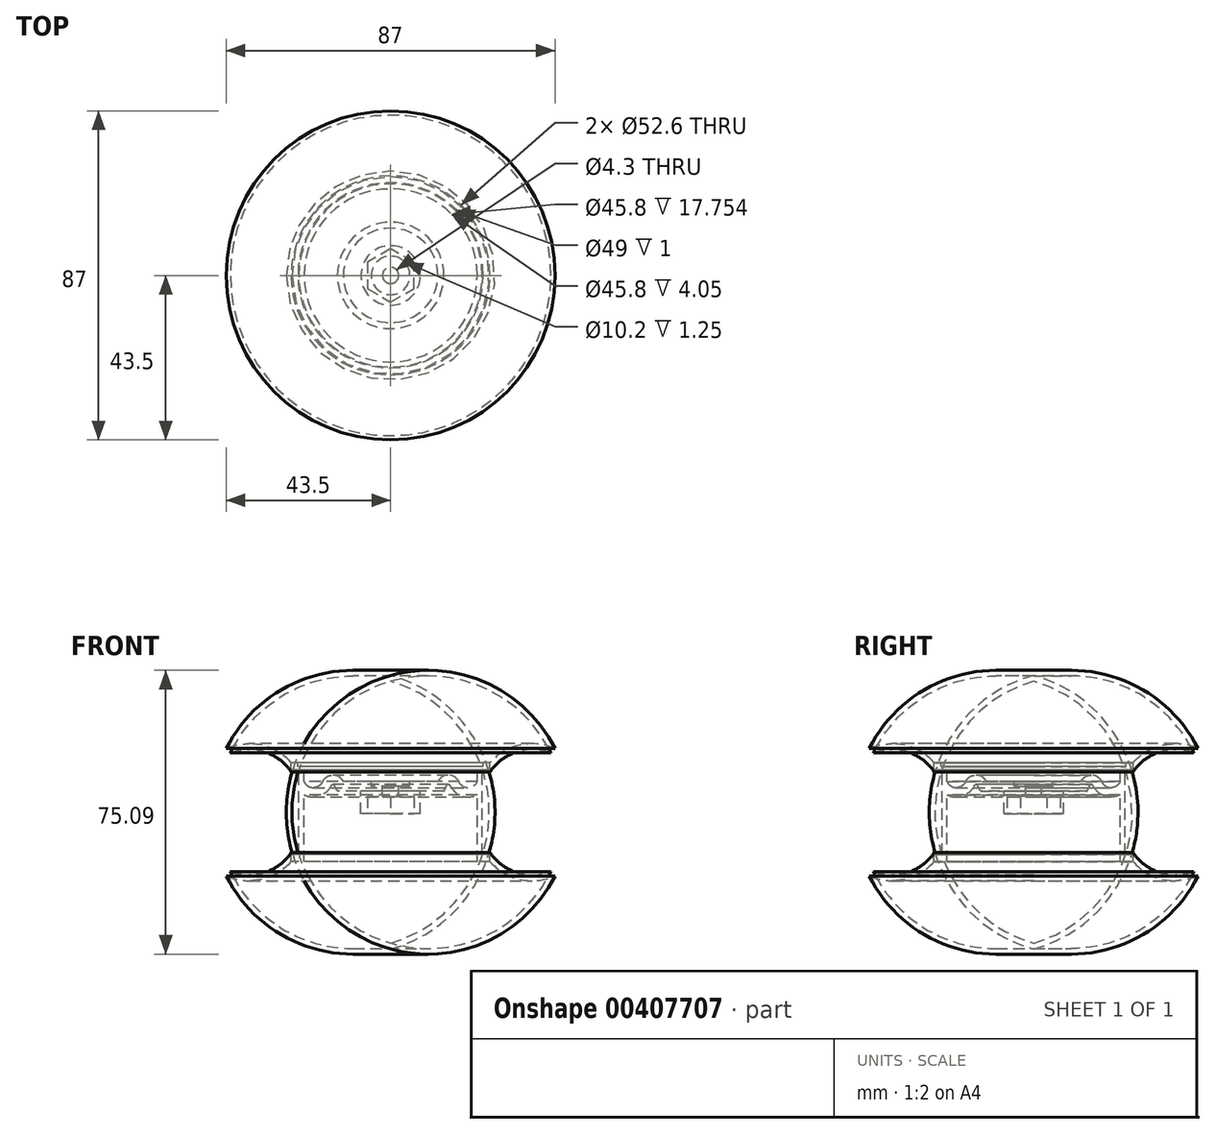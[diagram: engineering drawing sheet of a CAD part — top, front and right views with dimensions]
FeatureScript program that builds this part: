
annotation { "Feature Type Name" : "Feature", "Feature Type Description" : "" }
export const myFeature = defineFeature(function(context is Context, id is Id, definition is map)
    precondition{}
    {
        {
            var Q0;
            Q0=qCreatedBy(makeId("Front.planeOp"),FACE);
            var sketch = newSketch(context, id + "F0", { "sketchPlane" : qUnion([Q0])});
            skLineSegment(sketch, "E0", {"start": v(26.3, 0) * mm, "end": v(24.5, 0) * mm});
            skLineSegment(sketch, "E1", {"start": v(24.5, 0) * mm, "end": v(24.5, -1) * mm});
            skLineSegment(sketch, "E2", {"start": v(24.5, -1) * mm, "end": v(22.9, -1) * mm});
            skLineSegment(sketch, "E3", {"start": v(22.9, -1) * mm, "end": v(22.9, -26.25) * mm});
            skLineSegment(sketch, "E4", {"start": v(22.9, -26.25) * mm, "end": v(26.3, -26.25) * mm});
            skLineSegment(sketch, "E5", {"start": v(26.3, -26.25) * mm, "end": v(26.3, -24.35) * mm});
            skLineSegment(sketch, "E6", {"start": v(26.3, -24.35) * mm, "end": v(24.25, -24.35) * mm});
            skLineSegment(sketch, "E7", {"start": v(24.25, -24.35) * mm, "end": v(24.25, -1.9) * mm});
            skLineSegment(sketch, "E8", {"start": v(24.25, -1.9) * mm, "end": v(26.3, -1.9) * mm});
            skLineSegment(sketch, "E9", {"start": v(26.3, -1.9) * mm, "end": v(26.3, 0) * mm});
            skLineSegment(sketch, "E10", {"start": v(0, 0) * mm, "end": v(0, -26.25) * mm});
            skSolve(sketch);
        }
        {
            var Q0;
            Q0=qCreatedBy(makeId("Front.planeOp"),FACE);
            var sketch = newSketch(context, id + "F1", { "sketchPlane" : qUnion([Q0])});
            skLineSegment(sketch, "E11", {"start": v(2.15, -13.55) * mm, "end": v(2.15, -6.3) * mm});
            skLineSegment(sketch, "E12", {"start": v(2.15, -6.3) * mm, "end": v(5.1, -6.3) * mm});
            skLineSegment(sketch, "E13", {"start": v(5.1, -6.3) * mm, "end": v(5.1, -5.05) * mm});
            skLineSegment(sketch, "E14", {"start": v(5.1, -5.05) * mm, "end": v(12.5, -5.05) * mm});
            skLineSegment(sketch, "E15", {"start": v(2.15, -13.55) * mm, "end": v(7.88, -13.55) * mm});
            skLineSegment(sketch, "E16", {"start": v(7.88, -13.55) * mm, "end": v(7.88, -7.55) * mm});
            skLineSegment(sketch, "E17", {"start": v(7.88, -7.55) * mm, "end": v(14.1, -7.55) * mm});
            skArc(sketch, "E18", {"start": v(18, -5.05) * mm, "mid": v(15.25, -3.3) * mm, "end": v(12.5, -5.05) * mm});
            skArc(sketch, "E19", {"start": v(18, -5.05) * mm, "mid": v(20.45, -6.6) * mm, "end": v(22.9, -5.05) * mm});
            skArc(sketch, "E20.0", {"start": v(15.74, -6.1) * mm, "mid": v(15.25, -5.8) * mm, "end": v(14.76, -6.1) * mm});
            skArc(sketch, "E20.1", {"start": v(15.74, -6.1) * mm, "mid": v(18.8, -8.84) * mm, "end": v(22.9, -8.5) * mm});
            skLineSegment(sketch, "E21", {"start": v(14.76, -6.1) * mm, "end": v(14.1, -7.55) * mm});
            skLineSegment(sketch, "E22", {"start": v(14.76, -6.1) * mm, "end": v(12.5, -5.05) * mm, "construction": true});
            skLineSegment(sketch, "E23", {"start": v(22.9, -5.05) * mm, "end": v(22.9, -8.5) * mm});
            skSolve(sketch);
        }
        {
            var Q0;
            Q0=makeQuery(id+"F0.imprint","IMPRINT",FACE,{"disambiguationData":[TD([[makeQuery(id+"F0.imprint","IMPRINT",EDGE,{"derivedFrom":sQuery(id+"F0.wireOp",EDGE,"E0")}),1.0]])]});
            var Q1;
            Q1=sQuery(id+"F0.wireOp",EDGE,"E10");
            revolve(context, id + "F2", {"entities" : qUnion([Q0]), "axis" : qUnion([Q1]), "revolveType" : RevolveType.FULL});
        }
        {
            var Q0;
            Q0 = qSketchRegion(id + "F1", true);
            var Q1;
            Q1=sQuery(id+"F0.wireOp",EDGE,"E10");
            revolve(context, id + "F3", {"operationType" : NewBodyOperationType.ADD, "entities" : qUnion([Q0]), "axis" : qUnion([Q1]), "revolveType" : RevolveType.FULL});
        }
        {
            var Q0;
            Q0=makeQuery(id+"F3.opRevolve","SWEPT_FACE",FACE,{"disambiguationData":[OSD([sQuery(id+"F1.wireOp",EDGE,"E15")])]});
            var sketch = newSketch(context, id + "F4", { "sketchPlane" : qUnion([Q0])});
            skCircle(sketch, "E24.cCircle", {"center": v(0, 0) * mm, "radius": 6.13 * mm, "construction": true});
            skLineSegment(sketch, "E24.0", {"start": v(0, 7.07) * mm, "end": v(6.13, 3.54) * mm});
            skLineSegment(sketch, "E24.1", {"start": v(6.12, 3.54) * mm, "end": v(6.12, -3.54) * mm});
            skLineSegment(sketch, "E24.2", {"start": v(6.12, -3.54) * mm, "end": v(0, -7.07) * mm});
            skLineSegment(sketch, "E24.3", {"start": v(0, -7.07) * mm, "end": v(-6.13, -3.54) * mm});
            skLineSegment(sketch, "E24.4", {"start": v(-6.13, -3.54) * mm, "end": v(-6.13, 3.54) * mm});
            skLineSegment(sketch, "E24.5", {"start": v(-6.12, 3.54) * mm, "end": v(0, 7.07) * mm});
            skPoint(sketch, "E24.0.midPoint", {"position": v(3.06, 5.3) * mm});
            skSolve(sketch);
        }
        {
            var Q0;
            Q0 = qSketchRegion(id + "F4", true);
            extrude(context, id + "F5", {"entities" : qUnion([Q0]), "operationType" : NewBodyOperationType.REMOVE, "oppositeDirection" : true, "depth" : 4.6 * mm});
        }
        {
            var Q0;
            Q0=qCreatedBy(makeId("Front.planeOp"),FACE);
            var sketch = newSketch(context, id + "F6", { "sketchPlane" : qUnion([Q0])});
            skArc(sketch, "E25", {"start": v(-26.3, 0) * mm, "mid": v(-34.3, 4.66) * mm, "end": v(-43.5, 3.74) * mm});
            skArc(sketch, "E26", {"start": v(-43.5, -29.99) * mm, "mid": v(-34.3, -30.9) * mm, "end": v(-26.3, -26.25) * mm});
            skLineSegment(sketch, "E27", {"start": v(24.5, 0) * mm, "end": v(26.3, 0) * mm});
            skLineSegment(sketch, "E28", {"start": v(-26.3, 0) * mm, "end": v(-24.5, 0) * mm, "construction": true});
            skLineSegment(sketch, "E29", {"start": v(-22.9, -26.25) * mm, "end": v(-26.3, -26.25) * mm, "construction": true});
            skLineSegment(sketch, "E30", {"start": v(26.3, -26.25) * mm, "end": v(22.9, -26.25) * mm});
            skArc(sketch, "E31", {"start": v(-43.5, 3.74) * mm, "mid": v(-47.5, -13.13) * mm, "end": v(-43.5, -29.99) * mm});
            skLineSegment(sketch, "E32", {"start": v(-43.5, -29.99) * mm, "end": v(-43.5, 3.74) * mm, "construction": true});
            skLineSegment(sketch, "E33", {"start": v(-37.48, -16.25) * mm, "end": v(-37.48, -10) * mm, "construction": true});
            skLineSegment(sketch, "E34", {"start": v(-26.3, 0) * mm, "end": v(-26.3, -26.25) * mm});
            skSolve(sketch);
        }
        {
            var Q0;
            Q0 = qSketchRegion(id + "F6", true);
            var Q1;
            Q1=sQuery(id+"F0.wireOp",EDGE,"E10");
            revolve(context, id + "F7", {"entities" : qUnion([Q0]), "axis" : qUnion([Q1]), "revolveType" : RevolveType.FULL});
        }
        {
            var Q0;
            Q0=makeQuery(id+"F7.opRevolve","SWEPT_FACE",FACE,{"disambiguationData":[OSD([sQuery(id+"F6.wireOp",EDGE,"E34")])]});
            shell(context, id + "F8", {"entities" : qUnion([Q0]), "thickness" : 1.5 * mm});
        }
    });
